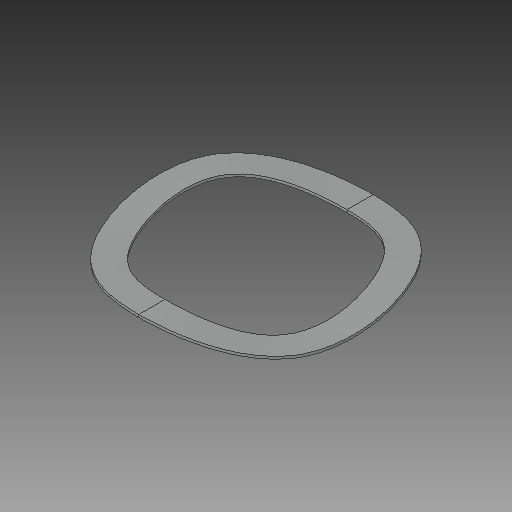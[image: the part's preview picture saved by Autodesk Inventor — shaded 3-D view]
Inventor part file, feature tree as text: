
AUTODESK INVENTOR PART (.ipt)
format: ipt  version: 2017 SP1 (Build 210196100, 196)  size: 122,368 bytes
history: native  units: in
note: dims shown in document units (in); Inventor stores cm internally (conversion verified against a paired STEP export)
features: loft x1
ambient origin geometry x8: Origin, YZ Plane, XZ Plane, XY Plane, X Axis, Y Axis, Z Axis, Center Point
bodies: Solid1 (feature_tree)
feature tree (1):
  loft  "Loft1"
